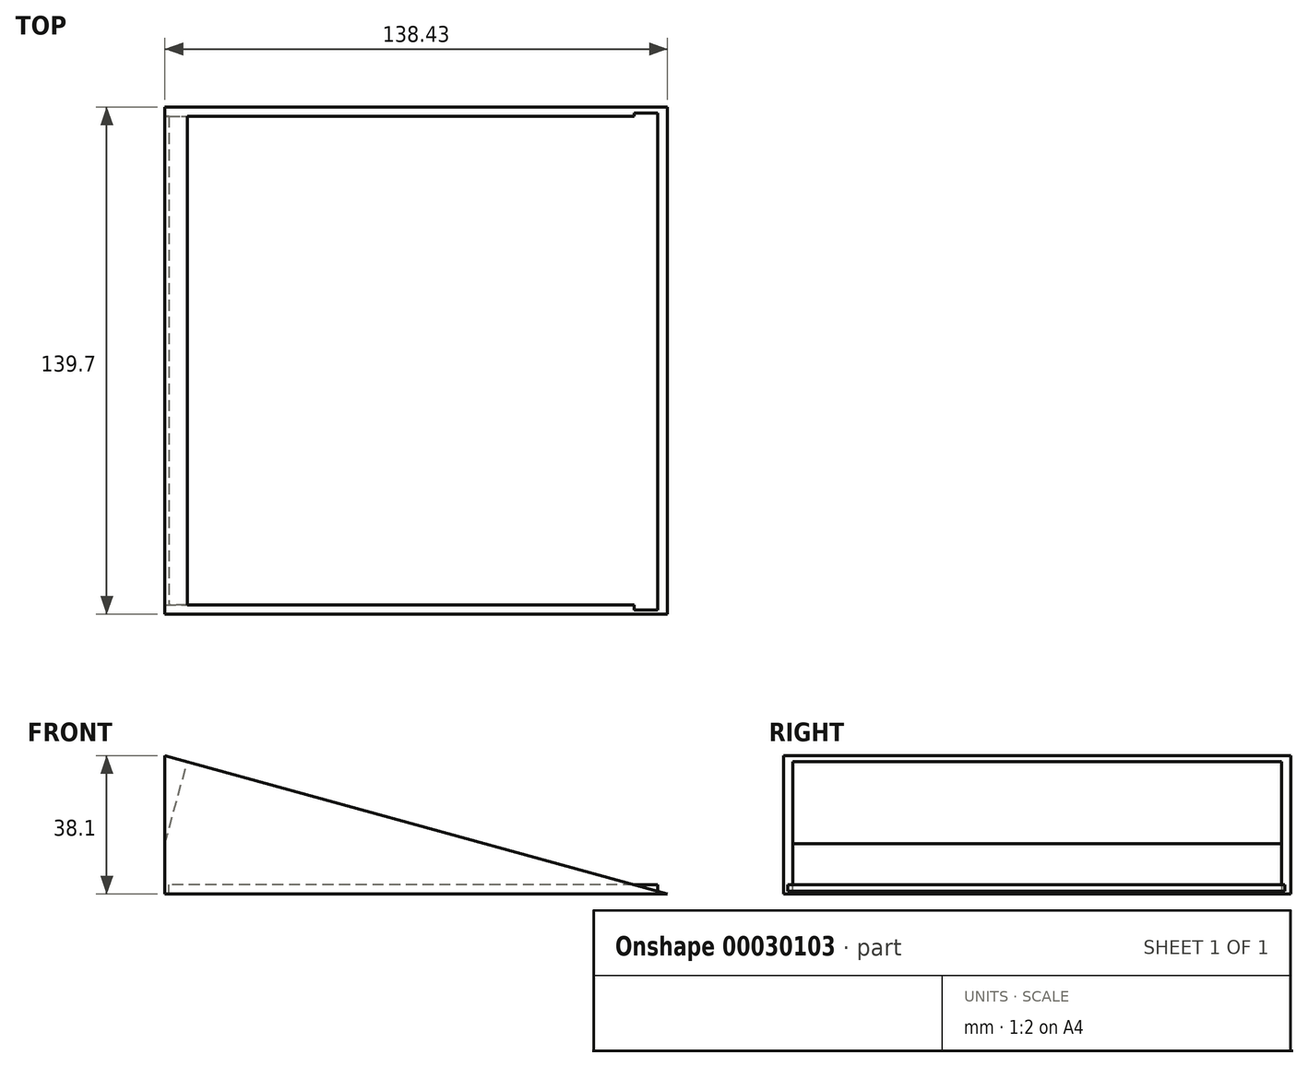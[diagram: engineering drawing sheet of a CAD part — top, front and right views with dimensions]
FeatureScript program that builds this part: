
annotation { "Feature Type Name" : "Feature", "Feature Type Description" : "" }
export const myFeature = defineFeature(function(context is Context, id is Id, definition is map)
    precondition{}
    {
        {
            var Q0;
            Q0=qCreatedBy(makeId("Top.planeOp"),FACE);
            var sketch = newSketch(context, id + "F0", { "sketchPlane" : qUnion([Q0])});
            skLineSegment(sketch, "E0.bottom", {"start": v(-79.42, -53.61) * mm, "end": v(59.01, -53.61) * mm});
            skLineSegment(sketch, "E0.top", {"start": v(-79.42, 86.09) * mm, "end": v(59.01, 86.09) * mm});
            skLineSegment(sketch, "E0.left", {"start": v(-79.42, -53.61) * mm, "end": v(-79.42, 86.09) * mm});
            skLineSegment(sketch, "E0.right", {"start": v(59.01, -53.61) * mm, "end": v(59.01, 86.09) * mm});
            skSolve(sketch);
        }
        {
            var Q0;
            Q0=makeQuery(id+"F0.imprint","IMPRINT",FACE,{"disambiguationData":[TD([[makeQuery(id+"F0.imprint","IMPRINT",EDGE,{"derivedFrom":sQuery(id+"F0.wireOp",EDGE,"E0.bottom")}),1.0]])]});
            extrude(context, id + "F1", {"entities" : qUnion([Q0]), "depth" : 38.1 * mm});
        }
        {
            var Q0;
            Q0=makeQuery(id+"F1.opExtrude","SWEPT_FACE",FACE,{"disambiguationData":[OSD([sQuery(id+"F0.wireOp",EDGE,"E0.bottom")])]});
            var sketch = newSketch(context, id + "F2", { "sketchPlane" : qUnion([Q0])});
            skLineSegment(sketch, "E1", {"start": v(-79.42, 38.1) * mm, "end": v(59.01, 0) * mm});
            skSolve(sketch);
        }
        {
            var Q0;
            Q0=makeQuery(id+"F2.imprint","IMPRINT",FACE,{"disambiguationData":[TD([[makeQuery(id+"F2.imprint","IMPRINT",EDGE,{"derivedFrom":sQuery(id+"F2.wireOp",EDGE,"E1")}),1.0]])]});
            extrude(context, id + "F3", {"entities" : qUnion([Q0]), "operationType" : NewBodyOperationType.REMOVE, "endBound" : BoundingType.THROUGH_ALL, "oppositeDirection" : true, "depth" : 25.4 * mm});
        }
        {
            var Q0;
            Q0=makeQuery(id+"F3.boolean.opBoolean","COPY",FACE,{"derivedFrom":makeQuery(id+"F3.opExtrude","SWEPT_FACE",FACE,{"disambiguationData":[OSD([sQuery(id+"F2.wireOp",EDGE,"E1")])]})});
            var sketch = newSketch(context, id + "F4", { "sketchPlane" : qUnion([Q0])});
            skLineSegment(sketch, "E2.0", {"start": v(-80.26, -51.07) * mm, "end": v(53.09, -51.07) * mm});
            skLineSegment(sketch, "E3.0", {"start": v(53.09, 83.55) * mm, "end": v(-80.26, 83.55) * mm});
            skLineSegment(sketch, "E4.0", {"start": v(53.09, -51.07) * mm, "end": v(53.09, 83.55) * mm});
            skLineSegment(sketch, "E5.0", {"start": v(-80.26, -51.07) * mm, "end": v(-80.26, 83.55) * mm});
            skSolve(sketch);
        }
        {
            var Q0;
            Q0=makeQuery(id+"F4.imprint","IMPRINT",FACE,{"disambiguationData":[TD([[makeQuery(id+"F4.imprint","IMPRINT",EDGE,{"derivedFrom":sQuery(id+"F4.wireOp",EDGE,"E2.0")}),1.0]])]});
            extrude(context, id + "F5", {"entities" : qUnion([Q0]), "operationType" : NewBodyOperationType.REMOVE, "endBound" : BoundingType.THROUGH_ALL, "oppositeDirection" : true, "depth" : 0.37 * mm});
        }
        {
            var Q0;
            Q0=qCreatedBy(makeId("Top.planeOp"),FACE);
            var sketch = newSketch(context, id + "F6", { "sketchPlane" : qUnion([Q0])});
            skLineSegment(sketch, "E6.bottom", {"start": v(56.33, 84.4) * mm, "end": v(-78.25, 84.4) * mm});
            skLineSegment(sketch, "E6.top", {"start": v(56.33, -52.49) * mm, "end": v(-78.25, -52.49) * mm});
            skLineSegment(sketch, "E6.left", {"start": v(56.33, 84.4) * mm, "end": v(56.33, -52.49) * mm});
            skLineSegment(sketch, "E6.right", {"start": v(-78.25, 84.4) * mm, "end": v(-78.25, -52.49) * mm});
            skSolve(sketch);
        }
        {
            var Q0;
            Q0 = qSketchRegion(id + "F6", true);
            extrude(context, id + "F7", {"entities" : qUnion([Q0]), "operationType" : NewBodyOperationType.ADD, "depth" : 2.54 * mm});
        }
    });
